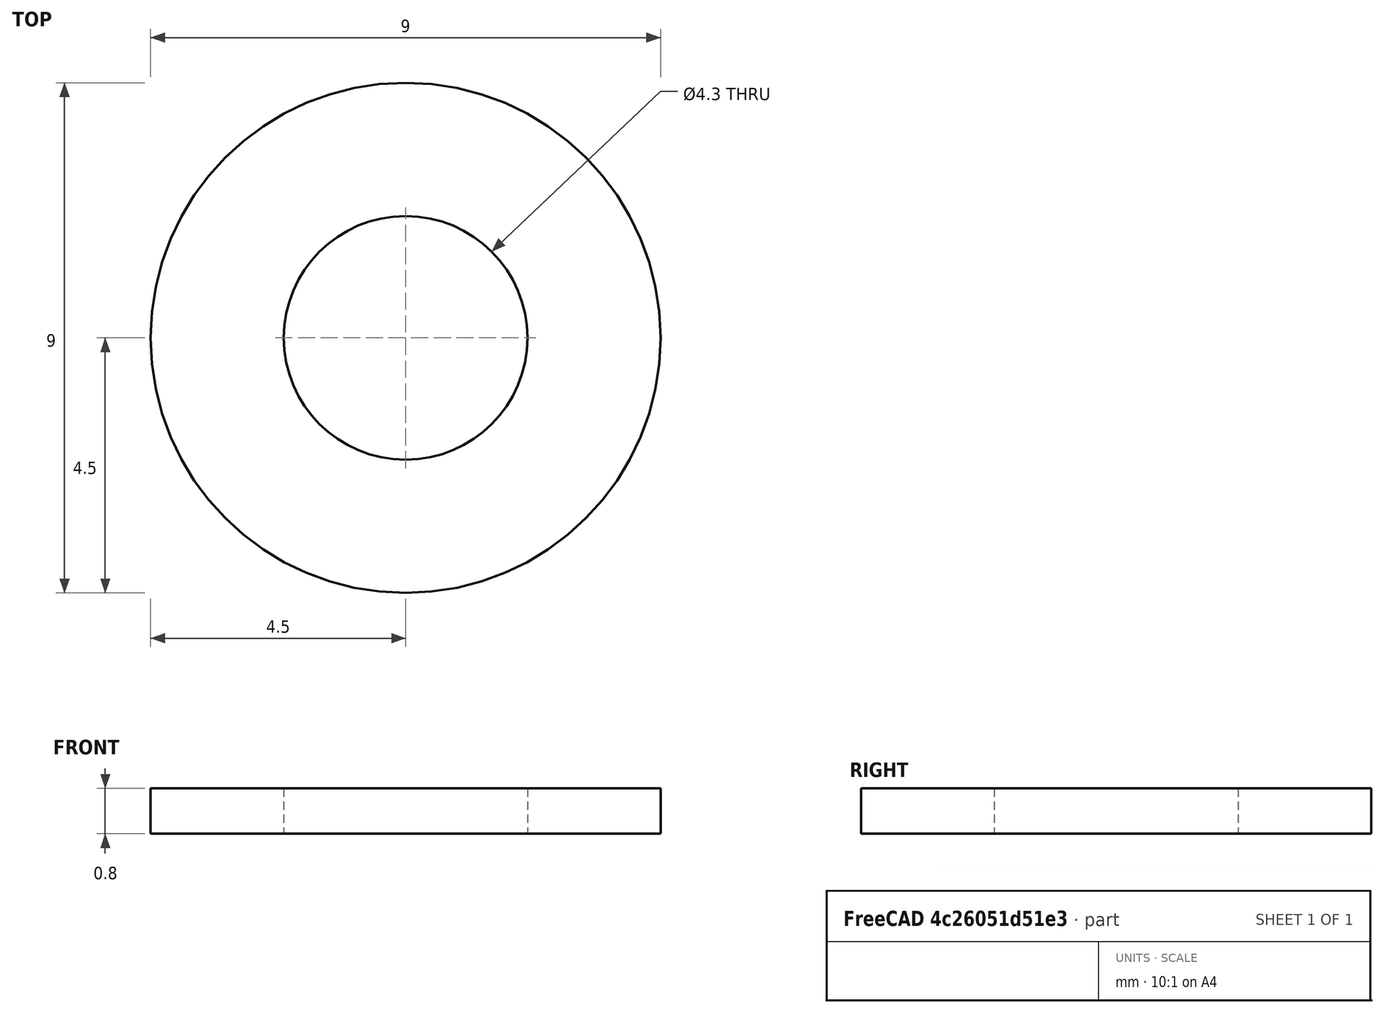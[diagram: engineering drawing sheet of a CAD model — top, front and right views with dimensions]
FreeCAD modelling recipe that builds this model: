
FCSTD DOCUMENT  (FreeCAD 0.14R3700 (Git))
Label: Scheibe DIN 125 - A 4,3
License: CC-BY 3.0
LicenseURL: http://creativecommons.org/licenses/by/3.0/
objects: Sketcher::SketchObject×1, PartDesign::Revolution×1, Part::Feature×1
note: 4 computed .brp shape members not serialized (recipe doc carries the construction recipe); baked Part::Feature solids carry a one-line shape summary decoded from their .brp

FEATURE [Sketcher::SketchObject] Sketch
  Placement = pos=(0,0,0) rot=(0.57735,0.57735,0.57735;2.0944rad)
  sketch-geometry (4):
    g0: LineSegment StartX=2.15 StartY=0 StartZ=0 EndX=4.5 EndY=0 EndZ=0
    g1: LineSegment StartX=4.5 StartY=0 StartZ=0 EndX=4.5 EndY=0.8 EndZ=0
    g2: LineSegment StartX=4.5 StartY=0.8 StartZ=0 EndX=2.15 EndY=0.8 EndZ=0
    g3: LineSegment StartX=2.15 StartY=0.8 StartZ=0 EndX=2.15 EndY=0 EndZ=0
  constraints (12):
    c: Coincident(g0,g1)
    c: Coincident(g1,g2)
    c: Coincident(g2,g3)
    c: Coincident(g3,g0)
    c: Horizontal(g0)
    c: Horizontal(g2)
    c: Vertical(g1)
    c: Vertical(g3)
    c: PointOnObject(g0,g-1)
    c: DistanceY(g1) = 0.8
    c: DistanceX(g-1,g2) = 2.15
    c: DistanceX(g-1,g1) = 4.5
FEATURE [PartDesign::Revolution] Revolution  label="Scheibe DIN 125 - A 4,3 #"
  Angle = 360
  Axis = (0,0,1)
  Base = (0,0,0)
  Placement = pos=(0,0,0) rot=(0.57735,0.57735,0.57735;2.0944rad)
  ReferenceAxis = -> Sketch [V_Axis]
  Reversed = true
  Sketch = -> Sketch
FEATURE [Part::Feature] Revolution001  label="Scheibe DIN 125 - A 4,3 #001"
  Placement = pos=(0,0,0) rot=(0.57735,0.57735,0.57735;2.0944rad)
  shape: bbox 9 x 9 x 0.8 mm, 4 faces (baked)
